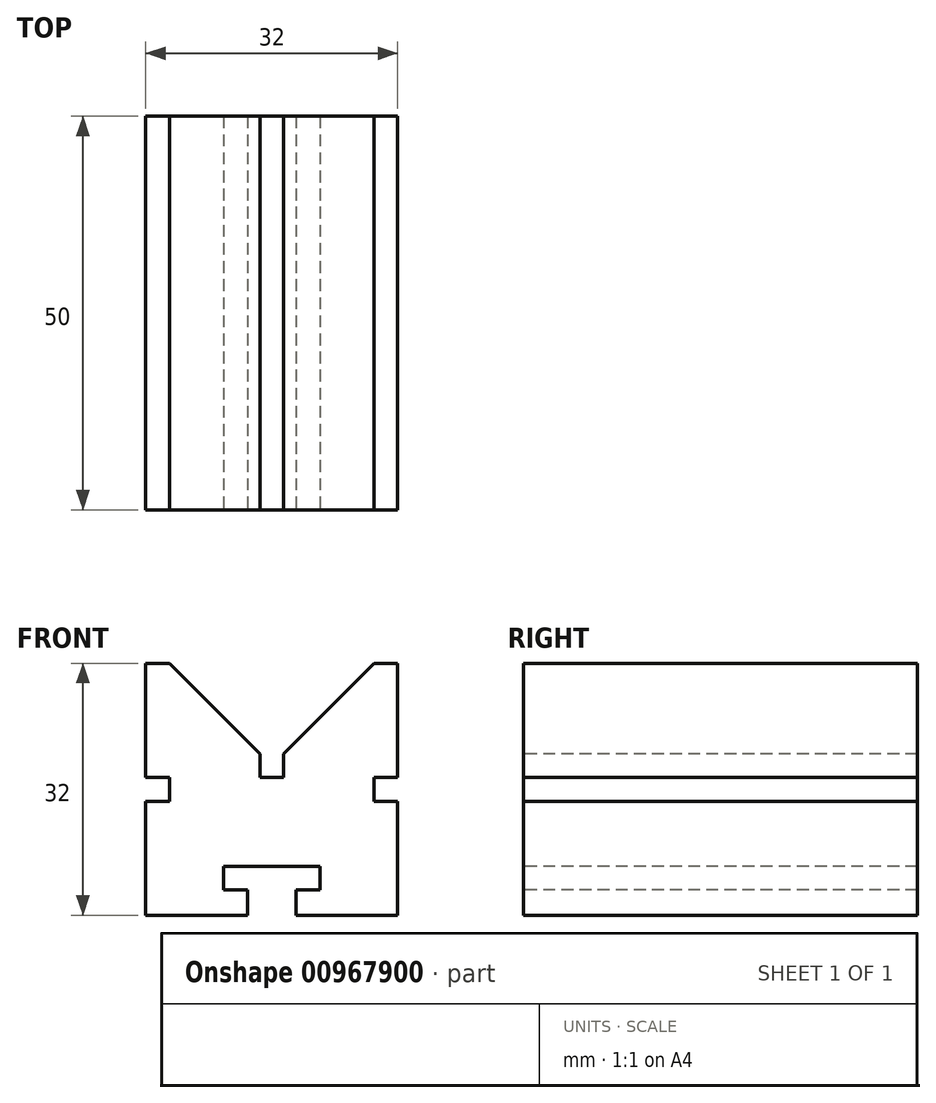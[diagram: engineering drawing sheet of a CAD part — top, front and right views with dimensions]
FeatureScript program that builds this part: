
annotation { "Feature Type Name" : "Feature", "Feature Type Description" : "" }
export const myFeature = defineFeature(function(context is Context, id is Id, definition is map)
    precondition{}
    {
        {
            var Q0;
            Q0=qCreatedBy(makeId("Front.planeOp"),FACE);
            var sketch = newSketch(context, id + "F0", { "sketchPlane" : qUnion([Q0])});
            skLineSegment(sketch, "E0.bottom", {"start": v(-16, 16) * mm, "end": v(-13, 16) * mm});
            skLineSegment(sketch, "E0.top", {"start": v(-16, -16) * mm, "end": v(16, -16) * mm});
            skLineSegment(sketch, "E0.left", {"start": v(-16, 16) * mm, "end": v(-16, -16) * mm});
            skLineSegment(sketch, "E0.right", {"start": v(16, 16) * mm, "end": v(16, -16) * mm});
            skPoint(sketch, "E0.middle", {"position": v(0, 0) * mm});
            skLineSegment(sketch, "E1", {"start": v(16, 16) * mm, "end": v(13, 16) * mm});
            skLineSegment(sketch, "E2", {"start": v(1.5, 1.5) * mm, "end": v(1.5, 4.5) * mm});
            skLineSegment(sketch, "E3", {"start": v(1.5, 4.5) * mm, "end": v(13, 16) * mm});
            skLineSegment(sketch, "E4", {"start": v(1.5, 1.5) * mm, "end": v(-1.5, 1.5) * mm});
            skLineSegment(sketch, "E5", {"start": v(-1.5, 1.5) * mm, "end": v(-1.5, 4.5) * mm});
            skLineSegment(sketch, "E6", {"start": v(-13, 16) * mm, "end": v(-1.5, 4.5) * mm});
            skLineSegment(sketch, "E7.trimOffspring", {"start": v(13, 16) * mm, "end": v(16, 16) * mm});
            skSolve(sketch);
        }
        {
            var Q0;
            Q0=makeQuery(id+"F0.imprint","IMPRINT",FACE,{"disambiguationData":[TD([[makeQuery(id+"F0.imprint","IMPRINT",EDGE,{"derivedFrom":sQuery(id+"F0.wireOp",EDGE,"E0.top")}),1.0]])]});
            extrude(context, id + "F1", {"entities" : qUnion([Q0]), "oppositeDirection" : true, "depth" : 50 * mm, "offsetDistance" : 25 * mm});
        }
        {
            var Q0;
            Q0=qCreatedBy(makeId("Front.planeOp"),FACE);
            var sketch = newSketch(context, id + "F2", { "sketchPlane" : qUnion([Q0])});
            skLineSegment(sketch, "E8", {"start": v(-6.1, -12.79) * mm, "end": v(-6.1, -9.79) * mm});
            skLineSegment(sketch, "E9", {"start": v(6.1, -12.79) * mm, "end": v(6.1, -9.79) * mm});
            skLineSegment(sketch, "E10", {"start": v(-6.1, -9.79) * mm, "end": v(6.1, -9.79) * mm});
            skPoint(sketch, "E11.orphan", {"position": v(3.1, -16.99) * mm});
            skPoint(sketch, "E12.end.orphan", {"position": v(0, -16.99) * mm});
            skLineSegment(sketch, "E13", {"start": v(-6.1, -12.79) * mm, "end": v(-3.1, -12.79) * mm});
            skLineSegment(sketch, "E14", {"start": v(-3.1, -16.99) * mm, "end": v(-3.1, -12.79) * mm});
            skLineSegment(sketch, "E15", {"start": v(3.1, -16.99) * mm, "end": v(3.1, -12.79) * mm});
            skLineSegment(sketch, "E16.trimOffspring", {"start": v(3.1, -12.79) * mm, "end": v(6.1, -12.79) * mm});
            skLineSegment(sketch, "E17", {"start": v(-3.1, -16.99) * mm, "end": v(3.1, -16.99) * mm});
            skLineSegment(sketch, "E18", {"start": v(15.9, 15.62) * mm, "end": v(15.9, 1.12) * mm});
            skLineSegment(sketch, "E19", {"start": v(15.9, 1.12) * mm, "end": v(15.9, -1.88) * mm});
            skLineSegment(sketch, "E20", {"start": v(-16, -1.88) * mm, "end": v(-13, -1.88) * mm});
            skLineSegment(sketch, "E21", {"start": v(-13, -1.88) * mm, "end": v(-13, 1.12) * mm});
            skLineSegment(sketch, "E22", {"start": v(15.9, -1.88) * mm, "end": v(12.9, -1.88) * mm});
            skLineSegment(sketch, "E23", {"start": v(12.9, -1.88) * mm, "end": v(12.9, 1.12) * mm});
            skLineSegment(sketch, "E24", {"start": v(-13, 1.12) * mm, "end": v(-16, 1.12) * mm});
            skLineSegment(sketch, "E25", {"start": v(12.9, 1.12) * mm, "end": v(15.9, 1.12) * mm});
            skSolve(sketch);
        }
        {
            var Q0;
            Q0=makeQuery(id+"F2.imprint","IMPRINT",FACE,{"disambiguationData":[TD([[makeQuery(id+"F2.imprint","IMPRINT",EDGE,{"derivedFrom":sQuery(id+"F2.wireOp",EDGE,"E8")}),-1.0]])]});
            extrude(context, id + "F3", {"entities" : qUnion([Q0]), "operationType" : NewBodyOperationType.REMOVE, "oppositeDirection" : true, "depth" : 55 * mm, "offsetDistance" : 25 * mm});
        }
        {
            var Q0;
            Q0=qCreatedBy(makeId("Front.planeOp"),FACE);
            var sketch = newSketch(context, id + "F4", { "sketchPlane" : qUnion([Q0])});
            skLineSegment(sketch, "E26", {"start": v(16, 16) * mm, "end": v(16, 1.5) * mm});
            skLineSegment(sketch, "E27", {"start": v(16, 1.5) * mm, "end": v(13, 1.5) * mm});
            skLineSegment(sketch, "E28", {"start": v(-16, 1.5) * mm, "end": v(-16, -1.5) * mm});
            skLineSegment(sketch, "E29", {"start": v(-16, -1.5) * mm, "end": v(16, -1.5) * mm});
            skLineSegment(sketch, "E30", {"start": v(16, -1.5) * mm, "end": v(16, 1.5) * mm});
            skLineSegment(sketch, "E31", {"start": v(-13, 1.5) * mm, "end": v(-13, -1.5) * mm});
            skLineSegment(sketch, "E32", {"start": v(13, 1.5) * mm, "end": v(13, -1.5) * mm});
            skLineSegment(sketch, "E33.trimOffspring", {"start": v(-13, 1.5) * mm, "end": v(-16, 1.5) * mm});
            skSolve(sketch);
        }
        {
            var Q0;
            Q0 = qSketchRegion(id + "F4", true);
            extrude(context, id + "F5", {"entities" : qUnion([Q0]), "operationType" : NewBodyOperationType.REMOVE, "oppositeDirection" : true, "depth" : 55 * mm, "offsetDistance" : 25 * mm});
        }
    });
